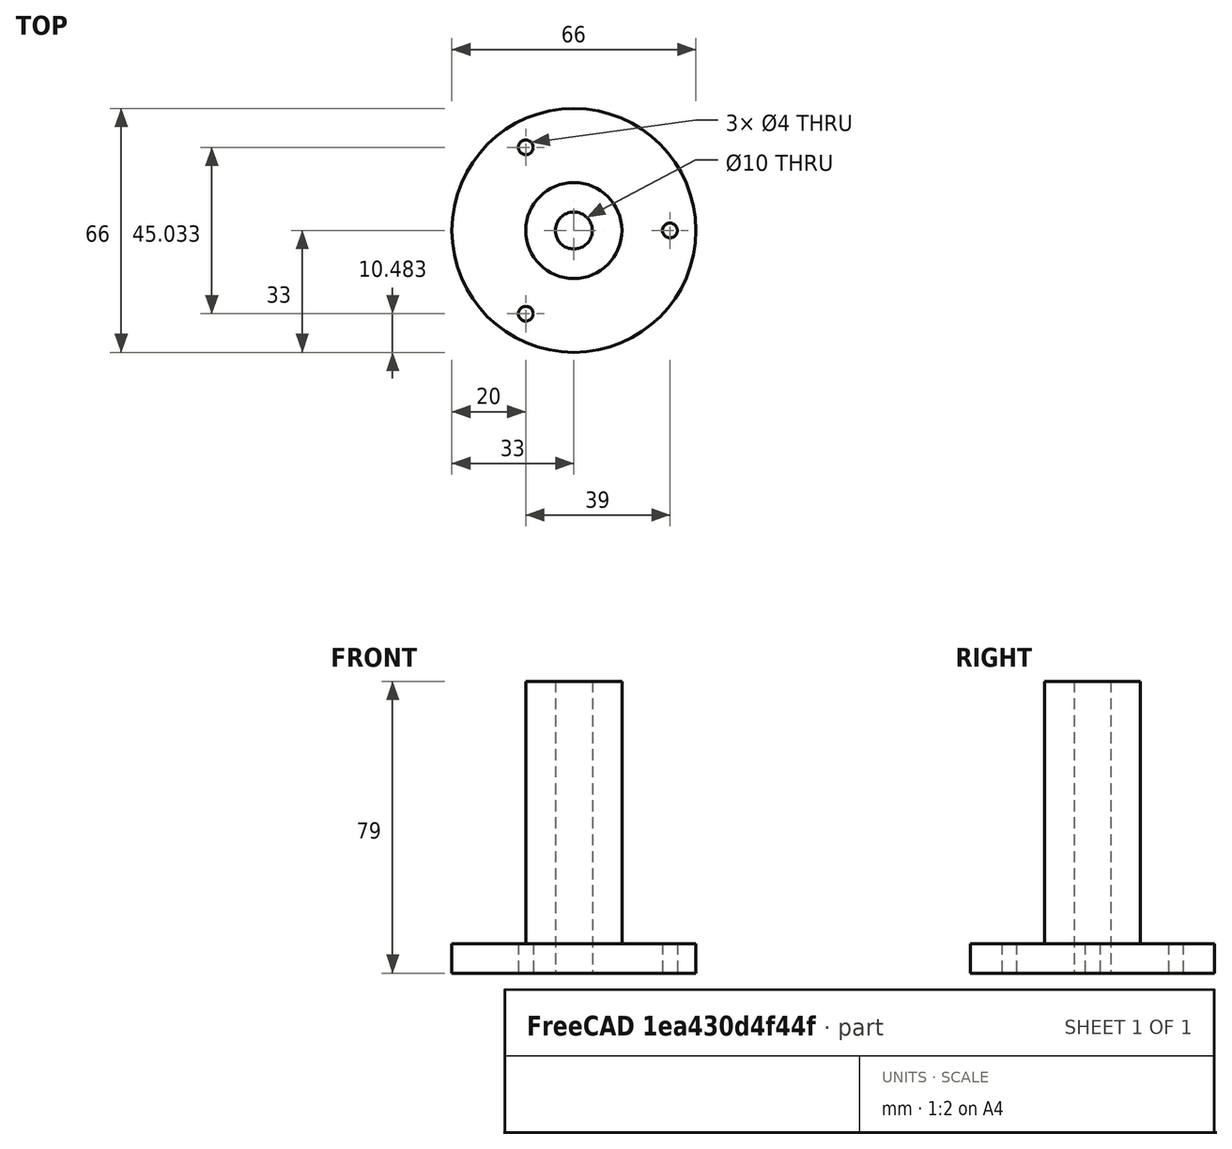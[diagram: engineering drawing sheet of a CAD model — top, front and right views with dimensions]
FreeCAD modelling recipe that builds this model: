
FCSTD DOCUMENT  (FreeCAD 1.1R38827 (Git))
Label: composit_stand3_sleeve_inner_main
License: All rights reserved
LicenseURL: http://en.wikipedia.org/wiki/All_rights_reserved
objects: Part::FeaturePython×2, Sketcher::SketchObject×1, Part::Feature×1
note: 5 computed .brp shape members not serialized (recipe doc carries the construction recipe); baked Part::Feature solids carry a one-line shape summary decoded from their .brp

FEATURE [Sketcher::SketchObject] Sketch  label="sleeve_inner_base_sketch"
  ArcFitTolerance = 0
  FullyConstrained = true
  MakeInternals = false
  Placement = pos=(0,0,0) rot=(1,0,0;1.5708rad)
  sketch-geometry (6):
    g0: LineSegment StartX=5 StartY=79 StartZ=0 EndX=5 EndY=0 EndZ=0
    g1: LineSegment StartX=5 StartY=0 StartZ=0 EndX=33 EndY=0 EndZ=0
    g2: LineSegment StartX=33 StartY=0 StartZ=0 EndX=33 EndY=8 EndZ=0
    g3: LineSegment StartX=33 StartY=8 StartZ=0 EndX=13 EndY=8 EndZ=0
    g4: LineSegment StartX=13 StartY=8 StartZ=0 EndX=13 EndY=79 EndZ=0
    g5: LineSegment StartX=13 StartY=79 StartZ=0 EndX=5 EndY=79 EndZ=0
  constraints (18):
    c: PointOnObject(g0,g-1)
    c: Vertical(g0)
    c: Coincident(g0,g1)
    c: PointOnObject(g1,g-1)
    c: Coincident(g1,g2)
    c: Vertical(g2)
    c: Coincident(g2,g3)
    c: Horizontal(g3)
    c: Coincident(g3,g4)
    c: Vertical(g4)
    c: Coincident(g4,g5)
    c: Coincident(g5,g0)
    c: Horizontal(g5)
    c: DistanceY(g2) = 8  'base_height'
    c: DistanceX(g0) = 5  'inner_r'
    c: DistanceX(g3) = 13  'outer_r'
    c: DistanceX(g1,g1) = 28  'bottom_r'
    c: DistanceY(g4,g4) = 71
FEATURE [Part::FeaturePython] PolarArray  # WARN: FeaturePython — macro-defined, semantics opaque (R4)
  Alignment = 0
  AttacherType = Attacher::AttachEngine3D
  CellStart = A1
  Count = 3
  DistributionLaw = 0
  EndInclusive = false
  ExposePlacement = false
  FlipX = false
  FlipZ = false
  GeneratorMode = 0
  MarkerShape = 1
  MarkerSize = 0
  NumElements = 3
  OrientMode = 2
  Placement = pos=(0,0,0) rot=(1,0,0;3.14159rad)
  Radius = 26
  Reverse = false
  SpanEnd = 360
  SpanStart = 0
  Step = 120
  Type = lattice2PolarArray2.PolarArray
  UseArcRadius = false
  UseArcRange = 0
  VSGVersion = 1
  Values = 0.0 | 120.0 | 240.0
  ValuesSource = 2
  isLattice = 1
FEATURE [Part::FeaturePython] Placment  # WARN: FeaturePython — macro-defined, semantics opaque (R4)
  AttacherType = Attacher::AttachEngine3D
  ExposePlacement = true
  MarkerShape = 1
  MarkerSize = 20
  NumElements = 1
  Type = lattice2AttachablePlacement.AttachablePlacement
  isLattice = 1
FEATURE [Part::Feature] Body169  label="sleeve_inner002"
  Placement = pos=(0,0,0) rot=(0,0,1;-0.523599rad)
  shape: bbox 66 x 66 x 79 mm, 9 faces (baked)
